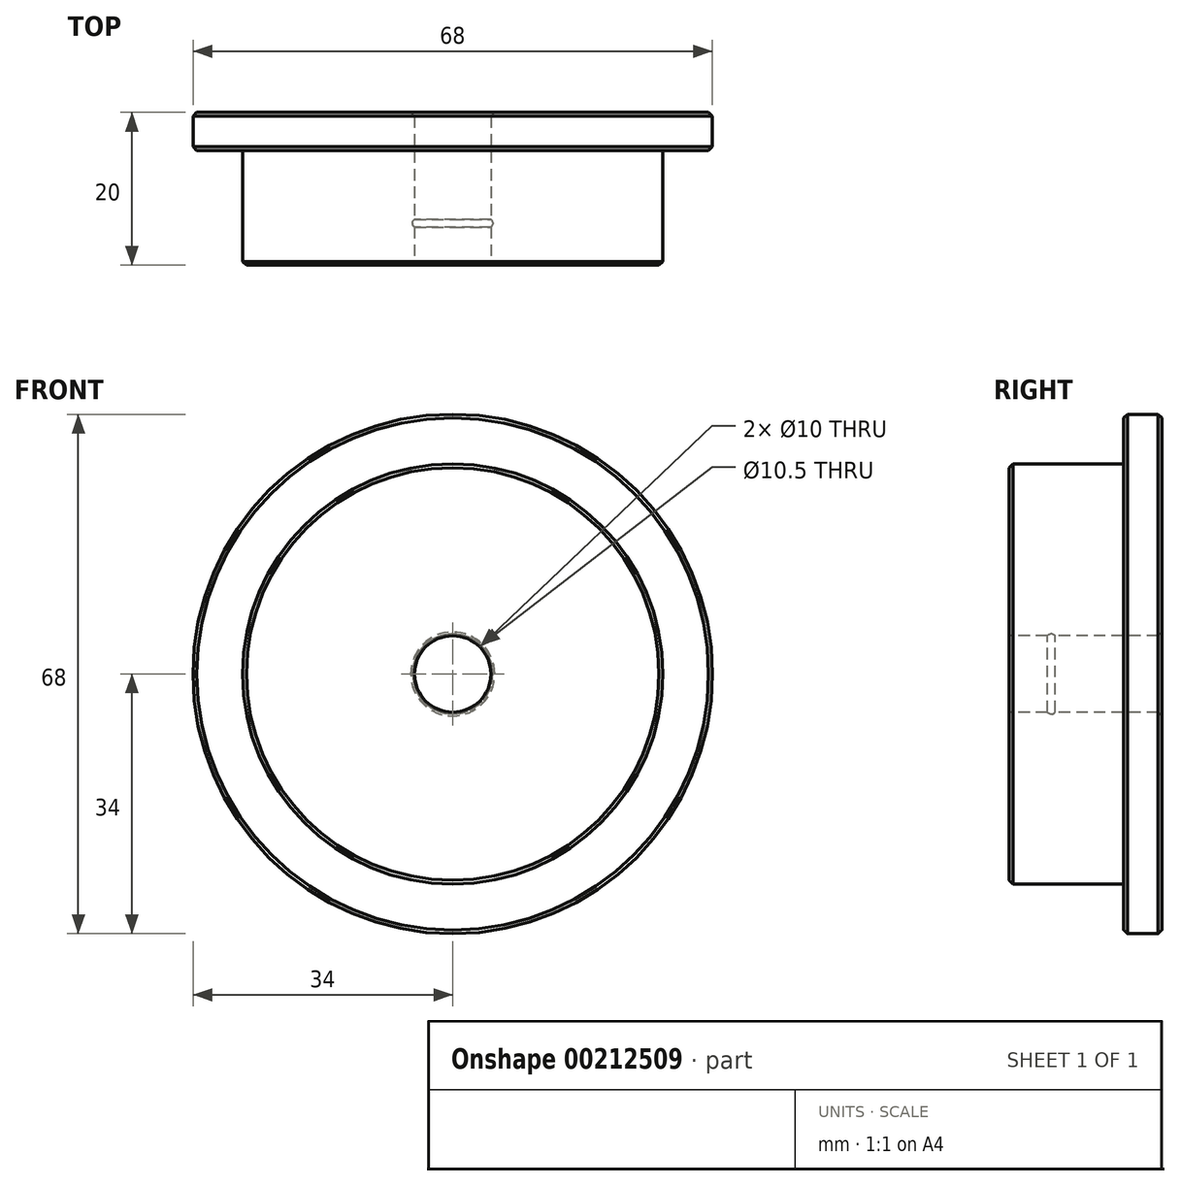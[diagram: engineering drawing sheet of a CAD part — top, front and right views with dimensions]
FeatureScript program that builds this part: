
annotation { "Feature Type Name" : "Feature", "Feature Type Description" : "" }
export const myFeature = defineFeature(function(context is Context, id is Id, definition is map)
    precondition{}
    {
        {
            var Q0;
            Q0=qCreatedBy(makeId("Front.planeOp"),FACE);
            var sketch = newSketch(context, id + "F0", { "sketchPlane" : qUnion([Q0])});
            skCircle(sketch, "E0", {"center": v(0, 0) * mm, "radius": 34 * mm});
            skSolve(sketch);
        }
        {
            var Q0;
            Q0 = qSketchRegion(id + "F0", true);
            extrude(context, id + "F1", {"entities" : qUnion([Q0]), "depth" : 5 * mm});
        }
        {
            var Q0;
            Q0=makeQuery(id+"F1.opExtrude","CAP_FACE",FACE,{"disambiguationData":[OSD([sQuery(id+"F0.wireOp",EDGE,"E0")])],"isStart":false});
            var sketch = newSketch(context, id + "F2", { "sketchPlane" : qUnion([Q0])});
            skCircle(sketch, "E1", {"center": v(0, 0) * mm, "radius": 27.5 * mm});
            skSolve(sketch);
        }
        {
            var Q0;
            Q0 = qSketchRegion(id + "F2", true);
            extrude(context, id + "F3", {"entities" : qUnion([Q0]), "operationType" : NewBodyOperationType.ADD, "depth" : 15 * mm});
        }
        {
            var Q0;
            Q0=makeQuery(id+"F3.opExtrude","CAP_FACE",FACE,{"disambiguationData":[OSD([sQuery(id+"F2.wireOp",EDGE,"E1")])],"isStart":false});
            var sketch = newSketch(context, id + "F4", { "sketchPlane" : qUnion([Q0])});
            skCircle(sketch, "E2", {"center": v(0, 0) * mm, "radius": 5 * mm});
            skSolve(sketch);
        }
        {
            var Q0;
            Q0 = qSketchRegion(id + "F4", true);
            extrude(context, id + "F5", {"entities" : qUnion([Q0]), "operationType" : NewBodyOperationType.REMOVE, "oppositeDirection" : true, "depth" : 30 * mm});
        }
        {
            var Q0;
            Q0=makeQuery(id+"F1.opExtrude","CAP_EDGE",EDGE,{"disambiguationData":[OSD([sQuery(id+"F0.wireOp",EDGE,"E0")])],"isStart":true});
            var Q1;
            Q1=makeQuery(id+"F3.opExtrude","CAP_EDGE",EDGE,{"disambiguationData":[OSD([sQuery(id+"F2.wireOp",EDGE,"E1")])],"isStart":false});
            var Q2;
            Q2=makeQuery(id+"F1.opExtrude","CAP_EDGE",EDGE,{"disambiguationData":[OSD([sQuery(id+"F0.wireOp",EDGE,"E0")])],"isStart":false});
            var Q3;
            Q3=makeQuery(id+"F3.opExtrude","CAP_EDGE",EDGE,{"disambiguationData":[OSD([sQuery(id+"F2.wireOp",EDGE,"E1")])],"isStart":true});
            var Q4;
            Q4=makeQuery(id+"F5.boolean.opBoolean","COPY",EDGE,{"derivedFrom":makeQuery(id+"F5.opExtrude","CAP_EDGE",EDGE,{"disambiguationData":[OSD([sQuery(id+"F4.wireOp",EDGE,"E2")])],"isStart":true})});
            var Q5;
            Q5=makeQuery(id+"F5.boolean.opBoolean","INTERSECT",EDGE,{"derivedFrom":[makeQuery(id+"F1.opExtrude","CAP_FACE",FACE,{"disambiguationData":[OSD([sQuery(id+"F0.wireOp",EDGE,"E0")])],"isStart":true}),makeQuery(id+"F5.opExtrude","SWEPT_FACE",FACE,{"disambiguationData":[OSD([sQuery(id+"F4.wireOp",EDGE,"E2")])]})]});
            chamfer(context, id + "F6", {"entities" : qUnion([Q0, Q1, Q2, Q3, Q4, Q5]), "width" : 0.5 * mm, "tangentPropagation" : true});
        }
        {
            var Q0;
            Q0=makeQuery(id+"F3.opExtrude","CAP_FACE",FACE,{"disambiguationData":[OSD([sQuery(id+"F2.wireOp",EDGE,"E1")])],"isStart":false});
            cPlane(context, id + "F7", {"entities" : qUnion([Q0]), "cplaneType" : CPlaneType.OFFSET, "offset" : 5 * mm, "oppositeDirection" : true, "width" : 150 * mm, "height" : 150 * mm});
        }
        {
            var Q0;
            Q0=qCreatedBy(id+"F7.planeOp",FACE);
            var sketch = newSketch(context, id + "F8", { "sketchPlane" : qUnion([Q0])});
            skCircle(sketch, "E3", {"center": v(0, 0) * mm, "radius": 5.25 * mm});
            skSolve(sketch);
        }
        {
            var Q0;
            Q0 = qSketchRegion(id + "F8", true);
            extrude(context, id + "F9", {"entities" : qUnion([Q0]), "operationType" : NewBodyOperationType.REMOVE, "oppositeDirection" : true, "depth" : 1 * mm});
        }
        {
            var Q0;
            Q0=makeQuery(id+"F9.boolean.opBoolean","COPY",FACE,{"derivedFrom":makeQuery(id+"F9.opExtrude","SWEPT_FACE",FACE,{"disambiguationData":[OSD([sQuery(id+"F8.wireOp",EDGE,"E3")])]})});
            fillet(context, id + "F10", {"entities" : qUnion([Q0]), "radius" : .5 * mm, "tangentPropagation" : true, "allowEdgeOverflow" : false});
        }
    });
